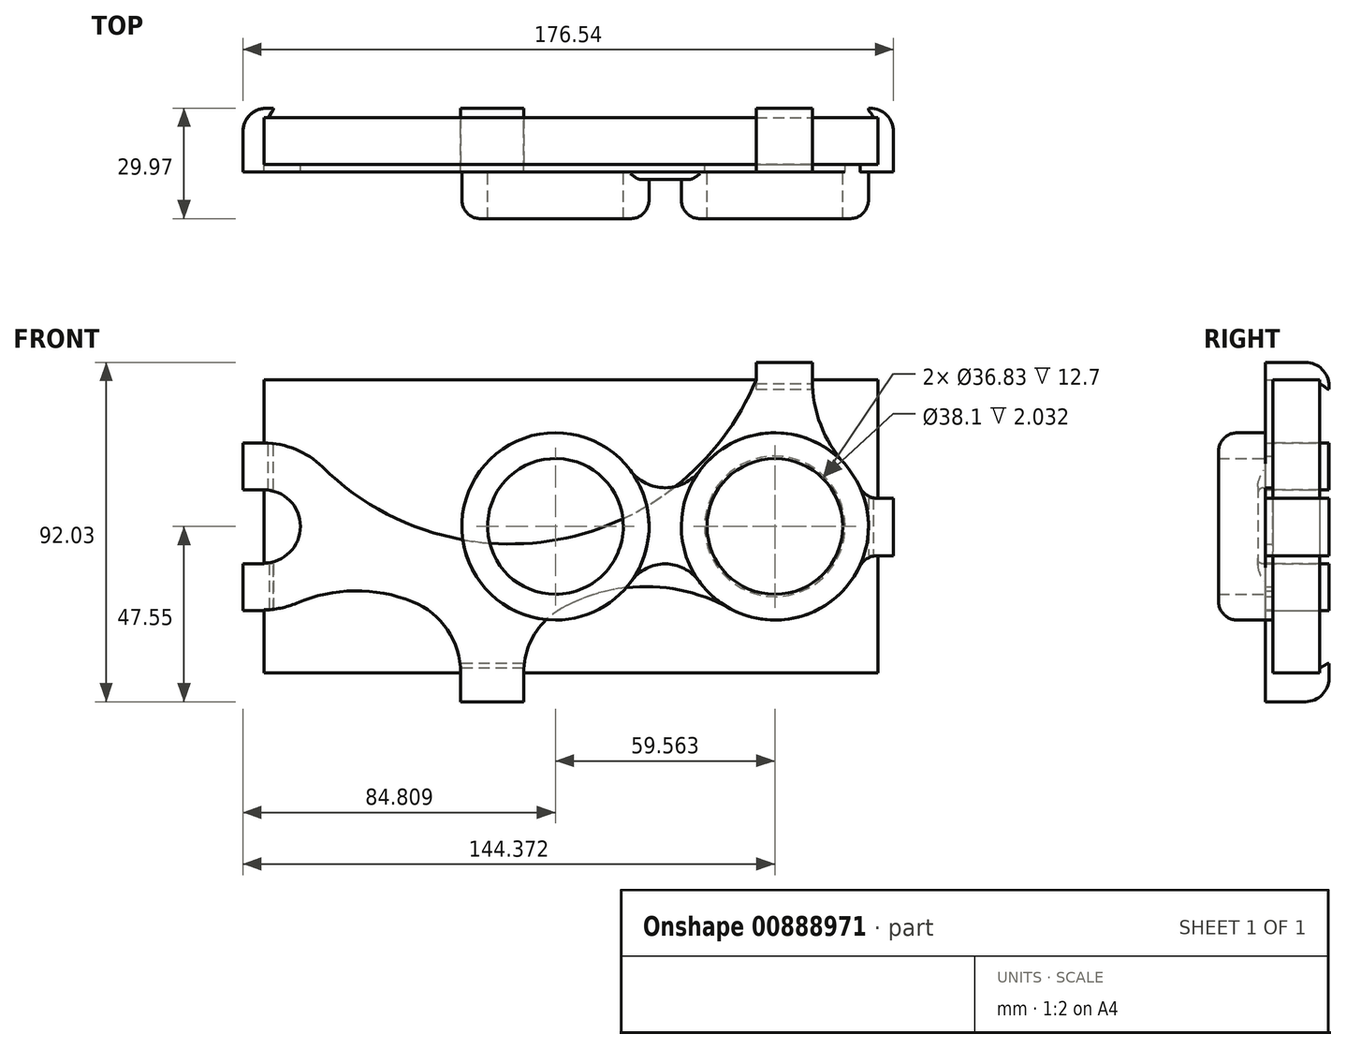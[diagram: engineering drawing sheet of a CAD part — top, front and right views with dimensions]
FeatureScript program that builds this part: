
annotation { "Feature Type Name" : "Feature", "Feature Type Description" : "" }
export const myFeature = defineFeature(function(context is Context, id is Id, definition is map)
    precondition{}
    {
        {
            var Q0;
            Q0=qCreatedBy(makeId("Front.planeOp"),FACE);
            var sketch = newSketch(context, id + "F0", { "sketchPlane" : qUnion([Q0])});
            skLineSegment(sketch, "E0.bottom", {"start": v(-83.31, 39.75) * mm, "end": v(83.31, 39.75) * mm});
            skLineSegment(sketch, "E0.top", {"start": v(-83.31, -39.75) * mm, "end": v(83.31, -39.75) * mm});
            skLineSegment(sketch, "E0.left", {"start": v(-83.31, 39.75) * mm, "end": v(-83.31, -39.75) * mm});
            skLineSegment(sketch, "E0.right", {"start": v(83.31, 39.75) * mm, "end": v(83.31, -39.75) * mm});
            skPoint(sketch, "E0.middle", {"position": v(0, 0) * mm});
            skSolve(sketch);
        }
        {
            var Q0;
            Q0 = qSketchRegion(id + "F0", true);
            extrude(context, id + "F1", {"entities" : qUnion([Q0]), "depth" : 12.7 * mm, "offsetDistance" : 25.4 * mm});
        }
        {
            var Q0;
            Q0=makeQuery(id+"F1.opExtrude","CAP_FACE",FACE,{"disambiguationData":[OSD([sQuery(id+"F0.wireOp",EDGE,"E0.bottom"),sQuery(id+"F0.wireOp",EDGE,"E0.top"),sQuery(id+"F0.wireOp",EDGE,"E0.left"),sQuery(id+"F0.wireOp",EDGE,"E0.right")])],"isStart":false});
            var sketch = newSketch(context, id + "F2", { "sketchPlane" : qUnion([Q0])});
            skCircle(sketch, "E1", {"center": v(55.37, 0) * mm, "radius": 2.35 * mm});
            skSolve(sketch);
        }
        {
            var Q0;
            Q0=makeQuery(id+"F2.imprint","IMPRINT",FACE,{"disambiguationData":[TD([[makeQuery(id+"F2.imprint","IMPRINT",EDGE,{"derivedFrom":sQuery(id+"F2.wireOp",EDGE,"E1")}),-1.0]])]});
            var sketch = newSketch(context, id + "F3", { "sketchPlane" : qUnion([Q0])});
            skPoint(sketch, "E2.0", {"position": v(55.37, 0) * mm});
            skCircle(sketch, "E3", {"center": v(55.37, 0) * mm, "radius": 19.05 * mm});
            skLineSegment(sketch, "E4.bottom", {"start": v(83.31, 7.62) * mm, "end": v(87.54, 7.62) * mm});
            skLineSegment(sketch, "E4.top", {"start": v(83.31, -7.95) * mm, "end": v(87.54, -7.95) * mm});
            skLineSegment(sketch, "E4.left", {"start": v(83.31, 7.62) * mm, "end": v(83.31, -7.95) * mm});
            skLineSegment(sketch, "E4.right", {"start": v(87.54, 7.62) * mm, "end": v(87.54, -7.95) * mm});
            skArc(sketch, "E5", {"start": v(43.05, -22.2) * mm, "mid": v(63, -24.23) * mm, "end": v(78.2, -11.14) * mm});
            skLineSegment(sketch, "E6.bottom", {"start": v(50.3, 39.75) * mm, "end": v(65.54, 39.75) * mm});
            skLineSegment(sketch, "E6.top", {"start": v(50.3, 44.48) * mm, "end": v(65.54, 44.48) * mm});
            skLineSegment(sketch, "E6.left", {"start": v(50.3, 39.75) * mm, "end": v(50.3, 44.48) * mm});
            skLineSegment(sketch, "E6.right", {"start": v(65.54, 39.75) * mm, "end": v(65.54, 44.48) * mm});
            skArc(sketch, "E7.trimOffspring", {"start": v(78.55, 10.4) * mm, "mid": v(76.66, 13.85) * mm, "end": v(74.27, 16.97) * mm});
            skLineSegment(sketch, "E8.left", {"start": v(-83.31, 22.62) * mm, "end": v(-83.31, 9.92) * mm});
            skLineSegment(sketch, "E9.left", {"start": v(-83.31, -10.16) * mm, "end": v(-83.31, -22.86) * mm});
            skArc(sketch, "E10", {"start": v(-83.31, 9.92) * mm, "mid": v(-73.4, 0) * mm, "end": v(-83.31, -9.92) * mm});
            skArc(sketch, "E11", {"start": v(-83.31, 22.62) * mm, "mid": v(-74.73, 20.93) * mm, "end": v(-67.43, 16.1) * mm});
            skLineSegment(sketch, "E12.bottom", {"start": v(-83.31, 22.62) * mm, "end": v(-89, 22.62) * mm});
            skLineSegment(sketch, "E12.top", {"start": v(-83.31, 9.92) * mm, "end": v(-89, 9.92) * mm});
            skLineSegment(sketch, "E12.right", {"start": v(-89, 22.62) * mm, "end": v(-89, 9.92) * mm});
            skLineSegment(sketch, "E13.bottom", {"start": v(-83.31, -10.16) * mm, "end": v(-89, -10.16) * mm});
            skLineSegment(sketch, "E13.top", {"start": v(-83.31, -22.86) * mm, "end": v(-89, -22.86) * mm});
            skLineSegment(sketch, "E13.right", {"start": v(-89, -10.16) * mm, "end": v(-89, -22.86) * mm});
            skLineSegment(sketch, "E14.bottom", {"start": v(-29.91, -39.75) * mm, "end": v(-12.83, -39.75) * mm});
            skLineSegment(sketch, "E14.top", {"start": v(-29.91, -47.55) * mm, "end": v(-12.83, -47.55) * mm});
            skLineSegment(sketch, "E14.left", {"start": v(-29.91, -39.75) * mm, "end": v(-29.91, -47.55) * mm});
            skLineSegment(sketch, "E14.right", {"start": v(-12.83, -39.75) * mm, "end": v(-12.83, -47.55) * mm});
            skArc(sketch, "E15", {"start": v(-29.91, -39.75) * mm, "mid": v(-33.49, -28.08) * mm, "end": v(-43, -20.42) * mm});
            skArc(sketch, "E16", {"start": v(-2.5, -22.2) * mm, "mid": v(-10.05, -29.57) * mm, "end": v(-12.83, -39.75) * mm});
            skArc(sketch, "E17", {"start": v(-43, -20.42) * mm, "mid": v(-58.74, -17.49) * mm, "end": v(-74.42, -20.8) * mm});
            skArc(sketch, "E18.trimOffspring", {"start": v(-74.42, -20.8) * mm, "mid": v(-78.77, -22.16) * mm, "end": v(-83.31, -22.62) * mm});
            skArc(sketch, "E19", {"start": v(43.05, -22.2) * mm, "mid": v(20.27, -16.31) * mm, "end": v(-2.5, -22.2) * mm});
            skArc(sketch, "E20", {"start": v(-67.43, 16.1) * mm, "mid": v(-2.3, -3.34) * mm, "end": v(50.3, 39.75) * mm});
            skArc(sketch, "E21", {"start": v(65.54, 39.75) * mm, "mid": v(67.8, 27.55) * mm, "end": v(74.27, 16.97) * mm});
            skArc(sketch, "E22", {"start": v(78.55, 10.4) * mm, "mid": v(80.55, 8.37) * mm, "end": v(83.31, 7.62) * mm});
            skArc(sketch, "E23", {"start": v(83.31, -7.95) * mm, "mid": v(80.3, -8.8) * mm, "end": v(78.2, -11.14) * mm});
            skSolve(sketch);
        }
        {
            var Q0;
            Q0=makeQuery(id+"F3.imprint","IMPRINT",FACE,{"disambiguationData":[TD([[makeQuery(id+"F3.imprint","IMPRINT",EDGE,{"derivedFrom":sQuery(id+"F3.wireOp",EDGE,"E3")}),-1.0]])]});
            var Q1;
            Q1=makeQuery(id+"F3.imprint","IMPRINT",FACE,{"disambiguationData":[TD([[makeQuery(id+"F3.imprint","IMPRINT",EDGE,{"derivedFrom":sQuery(id+"F3.wireOp",EDGE,"E6.bottom")}),1.0]])]});
            var Q2;
            Q2=makeQuery(id+"F3.imprint","IMPRINT",FACE,{"disambiguationData":[TD([[makeQuery(id+"F3.imprint","IMPRINT",EDGE,{"derivedFrom":sQuery(id+"F3.wireOp",EDGE,"E4.bottom")}),-1.0]])]});
            var Q3;
            Q3=makeQuery(id+"F3.imprint","IMPRINT",FACE,{"disambiguationData":[TD([[makeQuery(id+"F3.imprint","IMPRINT",EDGE,{"derivedFrom":sQuery(id+"F3.wireOp",EDGE,"E14.bottom")}),-1.0]])]});
            var Q4;
            {var subQ4=sQuery(id+"F3.wireOp",EDGE,"E13.bottom");Q4=makeQuery(id+"F3.imprint","IMPRINT",FACE,{"disambiguationData":[TD([[makeQuery(id+"F3.imprint","IMPRINT",EDGE,{"derivedFrom":subQ4}),1.0]])]});}
            var Q5;
            Q5=makeQuery(id+"F3.imprint","IMPRINT",FACE,{"disambiguationData":[TD([[makeQuery(id+"F3.imprint","IMPRINT",EDGE,{"derivedFrom":sQuery(id+"F3.wireOp",EDGE,"E12.bottom")}),1.0]])]});
            extrude(context, id + "F4", {"entities" : qUnion([Q0, Q1, Q2, Q3, Q4, Q5]), "depth" : 2.03 * mm, "offsetDistance" : 25.4 * mm});
        }
        {
            var Q0;
            {var subQ4=sQuery(id+"F3.wireOp",EDGE,"E13.bottom");Q0=makeQuery(id+"F3.imprint","IMPRINT",FACE,{"disambiguationData":[TD([[makeQuery(id+"F3.imprint","IMPRINT",EDGE,{"derivedFrom":subQ4}),1.0]])]});}
            var Q1;
            Q1=makeQuery(id+"F3.imprint","IMPRINT",FACE,{"disambiguationData":[TD([[makeQuery(id+"F3.imprint","IMPRINT",EDGE,{"derivedFrom":sQuery(id+"F3.wireOp",EDGE,"E12.bottom")}),1.0]])]});
            var Q2;
            Q2=makeQuery(id+"F3.imprint","IMPRINT",FACE,{"disambiguationData":[TD([[makeQuery(id+"F3.imprint","IMPRINT",EDGE,{"derivedFrom":sQuery(id+"F3.wireOp",EDGE,"E14.bottom")}),-1.0]])]});
            var Q3;
            Q3=makeQuery(id+"F3.imprint","IMPRINT",FACE,{"disambiguationData":[TD([[makeQuery(id+"F3.imprint","IMPRINT",EDGE,{"derivedFrom":sQuery(id+"F3.wireOp",EDGE,"E6.bottom")}),1.0]])]});
            var Q4;
            Q4=makeQuery(id+"F3.imprint","IMPRINT",FACE,{"disambiguationData":[TD([[makeQuery(id+"F3.imprint","IMPRINT",EDGE,{"derivedFrom":sQuery(id+"F3.wireOp",EDGE,"E4.bottom")}),-1.0]])]});
            extrude(context, id + "F5", {"entities" : qUnion([Q0, Q1, Q2, Q3, Q4]), "operationType" : NewBodyOperationType.ADD, "oppositeDirection" : true, "depth" : 15.24 * mm, "offsetDistance" : 25.4 * mm});
        }
        {
            var Q0;
            {var subQ0=sQuery(id+"F3.wireOp",EDGE,"E6.right");Q0=makeQuery(id+"F5.boolean.opBoolean","MERGE",FACE,{"derivedFrom":[makeQuery(id+"F4.opExtrude","SWEPT_FACE",FACE,{"disambiguationData":[OSD([subQ0])]}),makeQuery(id+"F5.opExtrude","SWEPT_FACE",FACE,{"disambiguationData":[OSD([subQ0])]})]});}
            var sketch = newSketch(context, id + "F6", { "sketchPlane" : qUnion([Q0])});
            skLineSegment(sketch, "E24", {"start": v(2.54, 37.21) * mm, "end": v(2.54, 39.75) * mm});
            skLineSegment(sketch, "E25", {"start": v(2.54, 39.75) * mm, "end": v(-5.08, 39.75) * mm});
            skFitSpline(sketch, "E26", {"points": [v(2.54, 37.21) * mm, v(-5.08, 39.75) * mm], "startDerivative": vector(-4, 0.03) * mm, "endDerivative": vector(-22.04, 2.26) * mm});
            skSolve(sketch);
        }
        {
            var Q0;
            Q0=makeQuery(id+"F6.imprint","IMPRINT",FACE,{"disambiguationData":[TD([[makeQuery(id+"F6.imprint","IMPRINT",EDGE,{"derivedFrom":sQuery(id+"F6.wireOp",EDGE,"E24")}),1.0]])]});
            var Q1;
            {var subQ0=sQuery(id+"F3.wireOp",EDGE,"E6.left");Q1=makeQuery(id+"F5.boolean.opBoolean","MERGE",FACE,{"derivedFrom":[makeQuery(id+"F4.opExtrude","SWEPT_FACE",FACE,{"disambiguationData":[OSD([subQ0])]}),makeQuery(id+"F5.opExtrude","SWEPT_FACE",FACE,{"disambiguationData":[OSD([subQ0])]})]});}
            extrude(context, id + "F7", {"entities" : qUnion([Q0]), "operationType" : NewBodyOperationType.ADD, "endBound" : BoundingType.UP_TO_SURFACE, "oppositeDirection" : true, "depth" : 25.4 * mm, "endBoundEntityFace" : qUnion([Q1]), "offsetDistance" : 25.4 * mm});
        }
        {
            var Q0;
            {var subQ0=sQuery(id+"F3.wireOp",EDGE,"E4.top");Q0=makeQuery(id+"F5.boolean.opBoolean","MERGE",FACE,{"derivedFrom":[makeQuery(id+"F4.opExtrude","SWEPT_FACE",FACE,{"disambiguationData":[OSD([subQ0])]}),makeQuery(id+"F5.opExtrude","SWEPT_FACE",FACE,{"disambiguationData":[OSD([subQ0])]})]});}
            var sketch = newSketch(context, id + "F8", { "sketchPlane" : qUnion([Q0])});
            skLineSegment(sketch, "E27", {"start": v(80.77, -2.54) * mm, "end": v(83.31, -2.54) * mm});
            skLineSegment(sketch, "E28", {"start": v(83.31, -2.54) * mm, "end": v(83.31, 5.08) * mm});
            skFitSpline(sketch, "E29", {"points": [v(80.77, -2.54) * mm, v(83.31, 5.08) * mm], "startDerivative": vector(0.08, 4.93) * mm, "endDerivative": vector(2.95, 21.77) * mm});
            skSolve(sketch);
        }
        {
            var Q0;
            Q0=makeQuery(id+"F8.imprint","IMPRINT",FACE,{"disambiguationData":[TD([[makeQuery(id+"F8.imprint","IMPRINT",EDGE,{"derivedFrom":sQuery(id+"F8.wireOp",EDGE,"E27")}),1.0]])]});
            var Q1;
            {var subQ0=sQuery(id+"F3.wireOp",EDGE,"E4.bottom");Q1=makeQuery(id+"F5.boolean.opBoolean","MERGE",FACE,{"derivedFrom":[makeQuery(id+"F4.opExtrude","SWEPT_FACE",FACE,{"disambiguationData":[OSD([subQ0])]}),makeQuery(id+"F5.opExtrude","SWEPT_FACE",FACE,{"disambiguationData":[OSD([subQ0])]})]});}
            extrude(context, id + "F9", {"entities" : qUnion([Q0]), "operationType" : NewBodyOperationType.ADD, "endBound" : BoundingType.UP_TO_SURFACE, "oppositeDirection" : true, "depth" : 25.4 * mm, "endBoundEntityFace" : qUnion([Q1]), "offsetDistance" : 25.4 * mm});
        }
        {
            var Q0;
            {var subQ0=sQuery(id+"F3.wireOp",EDGE,"E14.left");Q0=makeQuery(id+"F5.boolean.opBoolean","MERGE",FACE,{"derivedFrom":[makeQuery(id+"F4.opExtrude","SWEPT_FACE",FACE,{"disambiguationData":[OSD([subQ0])]}),makeQuery(id+"F5.opExtrude","SWEPT_FACE",FACE,{"disambiguationData":[OSD([subQ0])]})]});}
            var sketch = newSketch(context, id + "F10", { "sketchPlane" : qUnion([Q0])});
            skLineSegment(sketch, "E30", {"start": v(-2.54, -37.21) * mm, "end": v(-2.54, -39.75) * mm});
            skLineSegment(sketch, "E31", {"start": v(-2.54, -39.75) * mm, "end": v(5.08, -39.75) * mm});
            skFitSpline(sketch, "E32", {"points": [v(-2.54, -37.21) * mm, v(5.08, -39.75) * mm], "startDerivative": vector(3.73, 0.3) * mm, "endDerivative": vector(21.19, -3.81) * mm});
            skPoint(sketch, "E33", {"position": v(-2.54, -38.48) * mm});
            skSolve(sketch);
        }
        {
            var Q0;
            Q0=makeQuery(id+"F10.imprint","IMPRINT",FACE,{"disambiguationData":[TD([[makeQuery(id+"F10.imprint","IMPRINT",EDGE,{"derivedFrom":sQuery(id+"F10.wireOp",EDGE,"E30")}),1.0]])]});
            var Q1;
            {var subQ0=sQuery(id+"F3.wireOp",EDGE,"E14.right");Q1=makeQuery(id+"F5.boolean.opBoolean","MERGE",FACE,{"derivedFrom":[makeQuery(id+"F4.opExtrude","SWEPT_FACE",FACE,{"disambiguationData":[OSD([subQ0])]}),makeQuery(id+"F5.opExtrude","SWEPT_FACE",FACE,{"disambiguationData":[OSD([subQ0])]})]});}
            extrude(context, id + "F11", {"entities" : qUnion([Q0]), "operationType" : NewBodyOperationType.ADD, "endBound" : BoundingType.UP_TO_SURFACE, "oppositeDirection" : true, "depth" : 25.4 * mm, "endBoundEntityFace" : qUnion([Q1]), "offsetDistance" : 25.4 * mm});
        }
        {
            var Q0;
            {var subQ0=sQuery(id+"F3.wireOp",EDGE,"E13.top");Q0=makeQuery(id+"F5.boolean.opBoolean","MERGE",FACE,{"derivedFrom":[makeQuery(id+"F4.opExtrude","SWEPT_FACE",FACE,{"disambiguationData":[OSD([subQ0])]}),makeQuery(id+"F5.opExtrude","SWEPT_FACE",FACE,{"disambiguationData":[OSD([subQ0])]})]});}
            var sketch = newSketch(context, id + "F12", { "sketchPlane" : qUnion([Q0])});
            skLineSegment(sketch, "E34", {"start": v(-80.77, -2.54) * mm, "end": v(-83.31, -2.54) * mm});
            skLineSegment(sketch, "E35", {"start": v(-83.31, -2.54) * mm, "end": v(-83.31, 6.1) * mm});
            skFitSpline(sketch, "E36", {"points": [v(-80.77, -2.54) * mm, v(-83.31, 6.1) * mm], "startDerivative": vector(0.27, 4.37) * mm, "endDerivative": vector(-3.5, 24.44) * mm});
            skSolve(sketch);
        }
        {
            var Q0;
            Q0=makeQuery(id+"F12.imprint","IMPRINT",FACE,{"disambiguationData":[TD([[makeQuery(id+"F12.imprint","IMPRINT",EDGE,{"derivedFrom":sQuery(id+"F12.wireOp",EDGE,"E34")}),-1.0]])]});
            var Q1;
            {var subQ0=sQuery(id+"F3.wireOp",EDGE,"E13.bottom");Q1=makeQuery(id+"F5.boolean.opBoolean","MERGE",FACE,{"derivedFrom":[makeQuery(id+"F4.opExtrude","SWEPT_FACE",FACE,{"disambiguationData":[OSD([subQ0])]}),makeQuery(id+"F5.opExtrude","SWEPT_FACE",FACE,{"disambiguationData":[OSD([subQ0])]})]});}
            extrude(context, id + "F13", {"entities" : qUnion([Q0]), "operationType" : NewBodyOperationType.ADD, "endBound" : BoundingType.UP_TO_SURFACE, "oppositeDirection" : true, "depth" : 25.4 * mm, "endBoundEntityFace" : qUnion([Q1]), "offsetDistance" : 25.4 * mm});
        }
        {
            var Q0;
            {var subQ0=sQuery(id+"F3.wireOp",EDGE,"E12.bottom");Q0=makeQuery(id+"F5.boolean.opBoolean","MERGE",FACE,{"derivedFrom":[makeQuery(id+"F4.opExtrude","SWEPT_FACE",FACE,{"disambiguationData":[OSD([subQ0])]}),makeQuery(id+"F5.opExtrude","SWEPT_FACE",FACE,{"disambiguationData":[OSD([subQ0])]})]});}
            var sketch = newSketch(context, id + "F14", { "sketchPlane" : qUnion([Q0])});
            skLineSegment(sketch, "E37", {"start": v(-80.77, 2.45) * mm, "end": v(-83.31, 2.54) * mm});
            skLineSegment(sketch, "E38", {"start": v(-83.31, 2.54) * mm, "end": v(-83.31, -4.72) * mm});
            skFitSpline(sketch, "E39", {"points": [v(-80.77, 2.45) * mm, v(-83.31, -4.88) * mm], "startDerivative": vector(-0.26, -3.34) * mm, "endDerivative": vector(-3.25, -20.53) * mm});
            skSolve(sketch);
        }
        {
            var Q0;
            Q0=makeQuery(id+"F14.imprint","IMPRINT",FACE,{"disambiguationData":[TD([[makeQuery(id+"F14.imprint","IMPRINT",EDGE,{"derivedFrom":sQuery(id+"F14.wireOp",EDGE,"E37")}),1.0]])]});
            var Q1;
            {var subQ0=sQuery(id+"F3.wireOp",EDGE,"E12.top");Q1=makeQuery(id+"F5.boolean.opBoolean","MERGE",FACE,{"derivedFrom":[makeQuery(id+"F4.opExtrude","SWEPT_FACE",FACE,{"disambiguationData":[OSD([subQ0])]}),makeQuery(id+"F5.opExtrude","SWEPT_FACE",FACE,{"disambiguationData":[OSD([subQ0])]})]});}
            extrude(context, id + "F15", {"entities" : qUnion([Q0]), "operationType" : NewBodyOperationType.ADD, "endBound" : BoundingType.UP_TO_SURFACE, "oppositeDirection" : true, "depth" : 25.4 * mm, "endBoundEntityFace" : qUnion([Q1]), "offsetDistance" : 25.4 * mm});
        }
        {
            var Q0;
            Q0=makeQuery(id+"F5.opExtrude","CAP_EDGE",EDGE,{"disambiguationData":[OSD([sQuery(id+"F3.wireOp",EDGE,"E14.top")])],"isStart":false});
            var Q1;
            Q1=makeQuery(id+"F5.opExtrude","CAP_EDGE",EDGE,{"disambiguationData":[OSD([sQuery(id+"F3.wireOp",EDGE,"E13.right")])],"isStart":false});
            var Q2;
            Q2=makeQuery(id+"F5.opExtrude","CAP_EDGE",EDGE,{"disambiguationData":[OSD([sQuery(id+"F3.wireOp",EDGE,"E12.right")])],"isStart":false});
            var Q3;
            Q3=makeQuery(id+"F5.opExtrude","CAP_EDGE",EDGE,{"disambiguationData":[OSD([sQuery(id+"F3.wireOp",EDGE,"E4.right")])],"isStart":false});
            var Q4;
            Q4=makeQuery(id+"F5.opExtrude","CAP_EDGE",EDGE,{"disambiguationData":[OSD([sQuery(id+"F3.wireOp",EDGE,"E6.top")])],"isStart":false});
            fillet(context, id + "F16", {"entities" : qUnion([Q0, Q1, Q2, Q3, Q4]), "radius" : 6.35 * mm, "tangentPropagation" : true, "allowEdgeOverflow" : false});
        }
        {
            var Q0;
            Q0=makeQuery(id+"F4.opExtrude","CAP_FACE",FACE,{"disambiguationData":[OSD([sQuery(id+"F0.wireOp",EDGE,"E0.left"),sQuery(id+"F3.wireOp",EDGE,"E3"),sQuery(id+"F3.wireOp",EDGE,"E4.bottom"),sQuery(id+"F3.wireOp",EDGE,"E4.top"),sQuery(id+"F3.wireOp",EDGE,"E4.right"),sQuery(id+"F3.wireOp",EDGE,"E5"),sQuery(id+"F3.wireOp",EDGE,"E6.top"),sQuery(id+"F3.wireOp",EDGE,"E6.left"),sQuery(id+"F3.wireOp",EDGE,"E6.right"),sQuery(id+"F3.wireOp",EDGE,"E7.trimOffspring"),sQuery(id+"F3.wireOp",EDGE,"E10"),sQuery(id+"F3.wireOp",EDGE,"E11"),sQuery(id+"F3.wireOp",EDGE,"E12.bottom"),sQuery(id+"F3.wireOp",EDGE,"E12.top"),sQuery(id+"F3.wireOp",EDGE,"E12.right"),sQuery(id+"F3.wireOp",EDGE,"E13.bottom"),sQuery(id+"F3.wireOp",EDGE,"E13.top"),sQuery(id+"F3.wireOp",EDGE,"E9.left"),sQuery(id+"F3.wireOp",EDGE,"E13.right"),sQuery(id+"F3.wireOp",EDGE,"E14.top"),sQuery(id+"F3.wireOp",EDGE,"E14.left"),sQuery(id+"F3.wireOp",EDGE,"E14.right"),sQuery(id+"F3.wireOp",EDGE,"E15"),sQuery(id+"F3.wireOp",EDGE,"E16"),sQuery(id+"F3.wireOp",EDGE,"E17"),sQuery(id+"F3.wireOp",EDGE,"E18.trimOffspring"),sQuery(id+"F3.wireOp",EDGE,"E19"),sQuery(id+"F3.wireOp",EDGE,"E20"),sQuery(id+"F3.wireOp",EDGE,"E21"),sQuery(id+"F3.wireOp",EDGE,"E22"),sQuery(id+"F3.wireOp",EDGE,"E23")])],"isStart":false});
            var sketch = newSketch(context, id + "F17", { "sketchPlane" : qUnion([Q0])});
            skCircle(sketch, "E40", {"center": v(55.37, 0) * mm, "radius": 18.41 * mm});
            skCircle(sketch, "E41", {"center": v(-4.2, 0) * mm, "radius": 18.41 * mm});
            skCircle(sketch, "E42", {"center": v(55.37, 0) * mm, "radius": 25.4 * mm});
            skCircle(sketch, "E43", {"center": v(-4.2, 0) * mm, "radius": 25.4 * mm});
            skArc(sketch, "E44", {"start": v(16.16, 15.2) * mm, "mid": v(25.6, 10.48) * mm, "end": v(35.02, 15.2) * mm});
            skArc(sketch, "E45", {"start": v(34.78, -14.88) * mm, "mid": v(25.6, -10.18) * mm, "end": v(16.4, -14.88) * mm});
            skSolve(sketch);
        }
        {
            var Q0;
            {var subQ0=sQuery(id+"F17.wireOp",EDGE,"E45");Q0=makeQuery(id+"F17.imprint","IMPRINT",FACE,{"disambiguationData":[TD([[makeQuery(id+"F17.imprint","IMPRINT",EDGE,{"derivedFrom":subQ0}),-1.0]])]});}
            var Q1;
            {var subQ0=sQuery(id+"F17.wireOp",EDGE,"E44");var subQ1=sQuery(id+"F17.wireOp",EDGE,"E43");var subQ2=makeQuery(id+"F17.imprint","INTERSECT",VERTEX,{"derivedFrom":[subQ1,subQ0]});Q1=makeQuery(id+"F17.imprint","IMPRINT",FACE,{"disambiguationData":[TD([[makeQuery(id+"F17.imprint","IMPRINT",EDGE,{"disambiguationData":[TD([[subQ2,1.0]])],"derivedFrom":subQ1}),-1.0]])]});}
            extrude(context, id + "F18", {"entities" : qUnion([Q0, Q1]), "depth" : 2.03 * mm, "offsetDistance" : 25.4 * mm});
        }
        {
            var Q0;
            Q0=makeQuery(id+"F17.imprint","IMPRINT",FACE,{"disambiguationData":[TD([[makeQuery(id+"F17.imprint","IMPRINT",EDGE,{"derivedFrom":sQuery(id+"F17.wireOp",EDGE,"E40")}),-1.0]])]});
            var Q1;
            {var subQ2=makeQuery(id+"F4.opExtrude","CAP_EDGE",EDGE,{"disambiguationData":[OSD([sQuery(id+"F3.wireOp",EDGE,"E20")])],"isStart":false});var subQ6=sQuery(id+"F17.wireOp",EDGE,"E41");var subQ7=makeQuery(id+"F17.imprint","INTERSECT",VERTEX,{"disambiguationData":[OD(0.0)],"derivedFrom":[subQ2,subQ6]});Q1=makeQuery(id+"F17.imprint","IMPRINT",FACE,{"disambiguationData":[TD([[makeQuery(id+"F17.imprint","IMPRINT",EDGE,{"disambiguationData":[TD([[subQ7,-1.0]])],"derivedFrom":subQ6}),-1.0]])]});}
            var Q2;
            {var subQ1=makeQuery(id+"F4.opExtrude","CAP_EDGE",EDGE,{"disambiguationData":[OSD([sQuery(id+"F3.wireOp",EDGE,"E20")])],"isStart":false});var subQ3=sQuery(id+"F17.wireOp",EDGE,"E41");var subQ4=makeQuery(id+"F17.imprint","INTERSECT",VERTEX,{"disambiguationData":[OD(0.0)],"derivedFrom":[subQ1,subQ3]});Q2=makeQuery(id+"F17.imprint","IMPRINT",FACE,{"disambiguationData":[TD([[makeQuery(id+"F17.imprint","IMPRINT",EDGE,{"disambiguationData":[TD([[subQ4,1.0]])],"derivedFrom":subQ3}),-1.0]])]});}
            var Q3;
            {var subQ0=sQuery(id+"F17.wireOp",EDGE,"E43");var subQ1=makeQuery(id+"F4.opExtrude","CAP_EDGE",EDGE,{"disambiguationData":[OSD([sQuery(id+"F3.wireOp",EDGE,"E16")])],"isStart":false});var subQ2=makeQuery(id+"F17.imprint","INTERSECT",VERTEX,{"derivedFrom":[subQ1,subQ0]});Q3=makeQuery(id+"F17.imprint","IMPRINT",FACE,{"disambiguationData":[TD([[makeQuery(id+"F17.imprint","IMPRINT",EDGE,{"disambiguationData":[TD([[subQ2,-1.0]])],"derivedFrom":subQ0}),1.0]])]});}
            var Q4;
            Q4=makeQuery(id+"F17.imprint","IMPRINT",FACE,{"disambiguationData":[TD([[makeQuery(id+"F17.imprint","IMPRINT",EDGE,{"derivedFrom":makeQuery(id+"F4.opExtrude","CAP_EDGE",EDGE,{"disambiguationData":[OSD([sQuery(id+"F3.wireOp",EDGE,"E3")])],"isStart":false})}),-1.0]])]});
            extrude(context, id + "F19", {"entities" : qUnion([Q0, Q1, Q2, Q3, Q4]), "operationType" : NewBodyOperationType.ADD, "depth" : 12.7 * mm, "offsetDistance" : 25.4 * mm});
        }
        {
            var Q0;
            Q0=makeQuery(id+"F19.opExtrude","CAP_EDGE",EDGE,{"disambiguationData":[OSD([sQuery(id+"F17.wireOp",EDGE,"E42")])],"isStart":false});
            var Q1;
            Q1=makeQuery(id+"F19.opExtrude","CAP_EDGE",EDGE,{"disambiguationData":[OSD([sQuery(id+"F17.wireOp",EDGE,"E43")])],"isStart":false});
            fillet(context, id + "F20", {"entities" : qUnion([Q0, Q1]), "radius" : 5.08 * mm, "tangentPropagation" : true, "allowEdgeOverflow" : false});
        }
        {
            var Q0;
            Q0=makeQuery(id+"F18.opExtrude","CAP_EDGE",EDGE,{"disambiguationData":[OSD([sQuery(id+"F17.wireOp",EDGE,"E44")])],"isStart":false});
            var Q1;
            Q1=makeQuery(id+"F18.opExtrude","CAP_EDGE",EDGE,{"disambiguationData":[OSD([sQuery(id+"F17.wireOp",EDGE,"E45")])],"isStart":false});
            fillet(context, id + "F21", {"entities" : qUnion([Q0, Q1]), "radius" : 1.52 * mm, "tangentPropagation" : true, "allowEdgeOverflow" : false});
        }
    });
